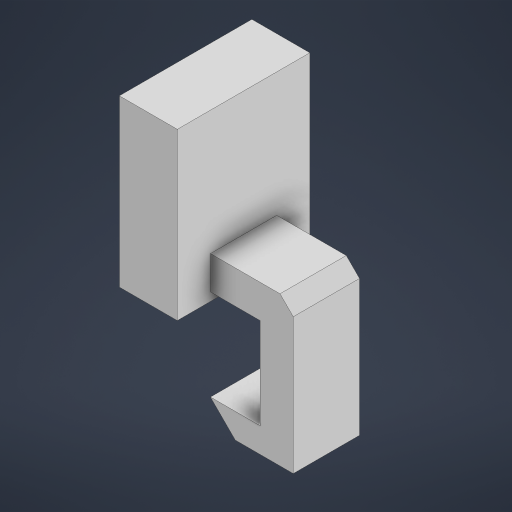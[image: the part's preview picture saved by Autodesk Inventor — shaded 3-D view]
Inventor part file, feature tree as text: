
AUTODESK INVENTOR PART (.ipt)
format: ipt  version: 2024.1 (Build 281209000, 209)  size: 206,336 bytes
history: native  units: mm
features: extrude x4, sketch x4, chamfer x2
ambient origin geometry x8: Origin, YZ Plane, XZ Plane, XY Plane, X Axis, Y Axis, Z Axis, Center Point
bodies: Solid1 (feature_tree)
feature tree (10):
  extrude  "Extrusion1"  Depth=8.0mm
  extrude  "Extrusion2"  Depth=2.0mm
  extrude  "Extrusion3"  Depth=2.0mm
  chamfer  "Chamfer1"  Distance=5.0mm
  extrude  "Extrusion6"  Depth=7.0mm TaperAngle=0.0deg
  chamfer  "Chamfer2"  Distance=2.0mm Angle=45.0deg
  sketch  "Sketch1"  dims[d0=3.5mm d1=8.0mm]
  sketch  "Sketch2"  dims[d2=10.0mm d3=0.0mm d4=2.0mm]
  sketch  "Sketch3"  dims[d5=4.0mm d6=2.0mm]
  sketch  "Sketch6"  dims[d7=0.5mm d8=5.0mm d9=0.0mm d10=7.0mm d11=0.0mm d19=0.8mm d20=2.0mm d21=45.0deg d22=2.0mm d23=1.5mm d24=3.0mm d25=0.0mm d26=1.5mm d27=2.0mm d28=45.0deg]
